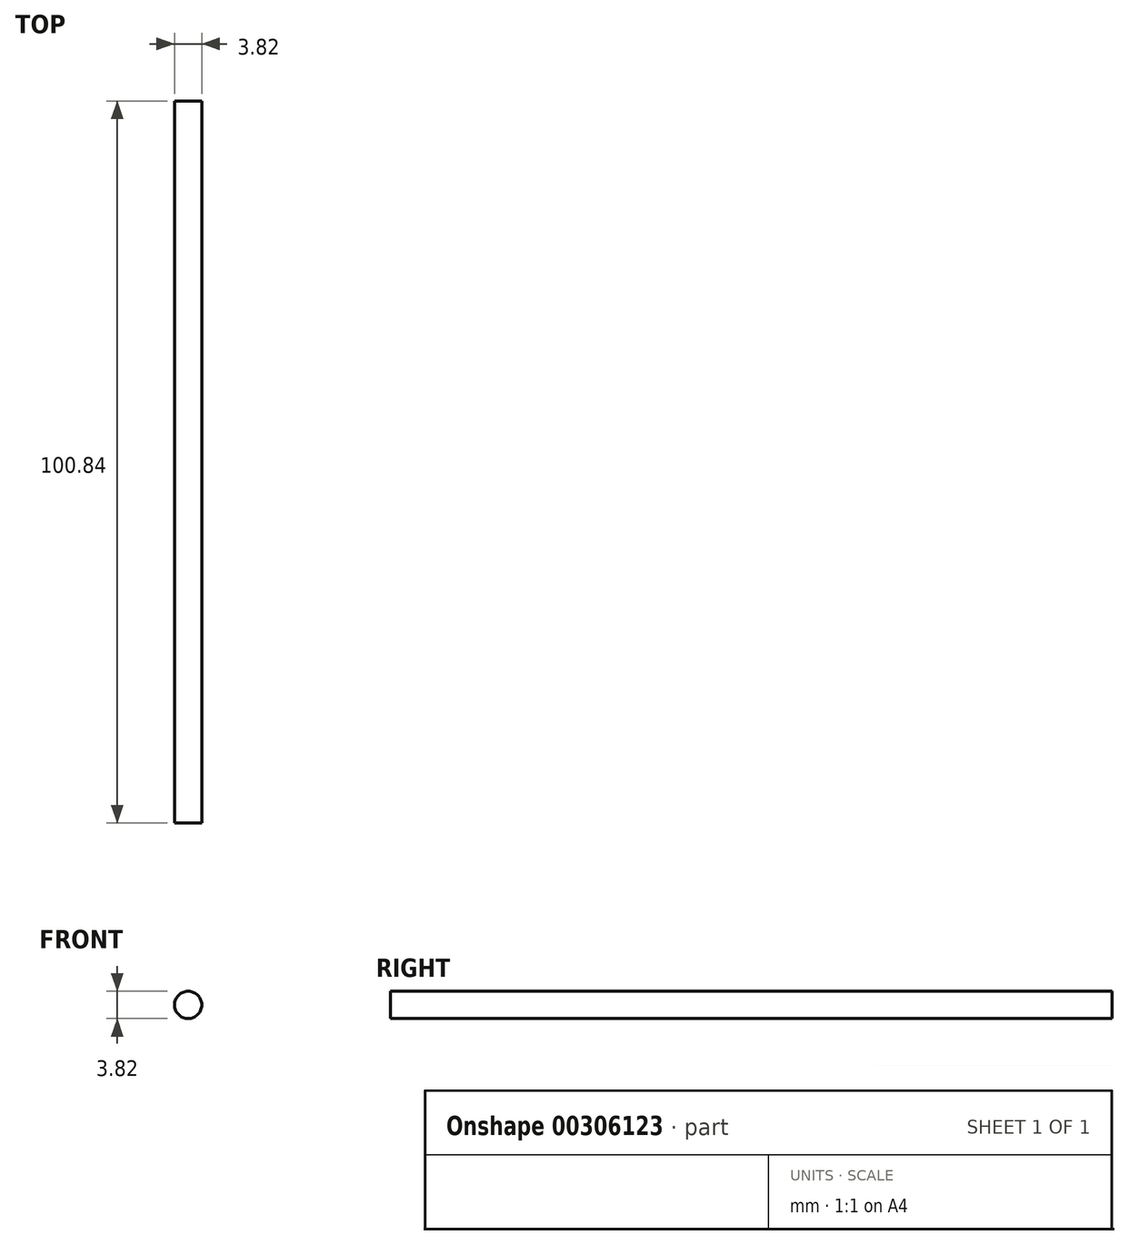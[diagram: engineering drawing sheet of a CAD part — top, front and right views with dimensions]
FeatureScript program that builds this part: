
annotation { "Feature Type Name" : "Feature", "Feature Type Description" : "" }
export const myFeature = defineFeature(function(context is Context, id is Id, definition is map)
    precondition{}
    {
        {
            var Q0;
            Q0=qCreatedBy(makeId("Front.planeOp"),FACE);
            var sketch = newSketch(context, id + "F0", { "sketchPlane" : qUnion([Q0])});
            skCircle(sketch, "E0", {"center": v(0, 0) * mm, "radius": 1.9 * mm});
            skSolve(sketch);
        }
        {
            var Q0;
            Q0 = qSketchRegion(id + "F0", true);
            extrude(context, id + "F1", {"entities" : qUnion([Q0]), "depth" : 69.6 * mm, "hasSecondDirection" : true, "secondDirectionOppositeDirection" : true, "secondDirectionDepth" : 31.24 * mm});
        }
    });
